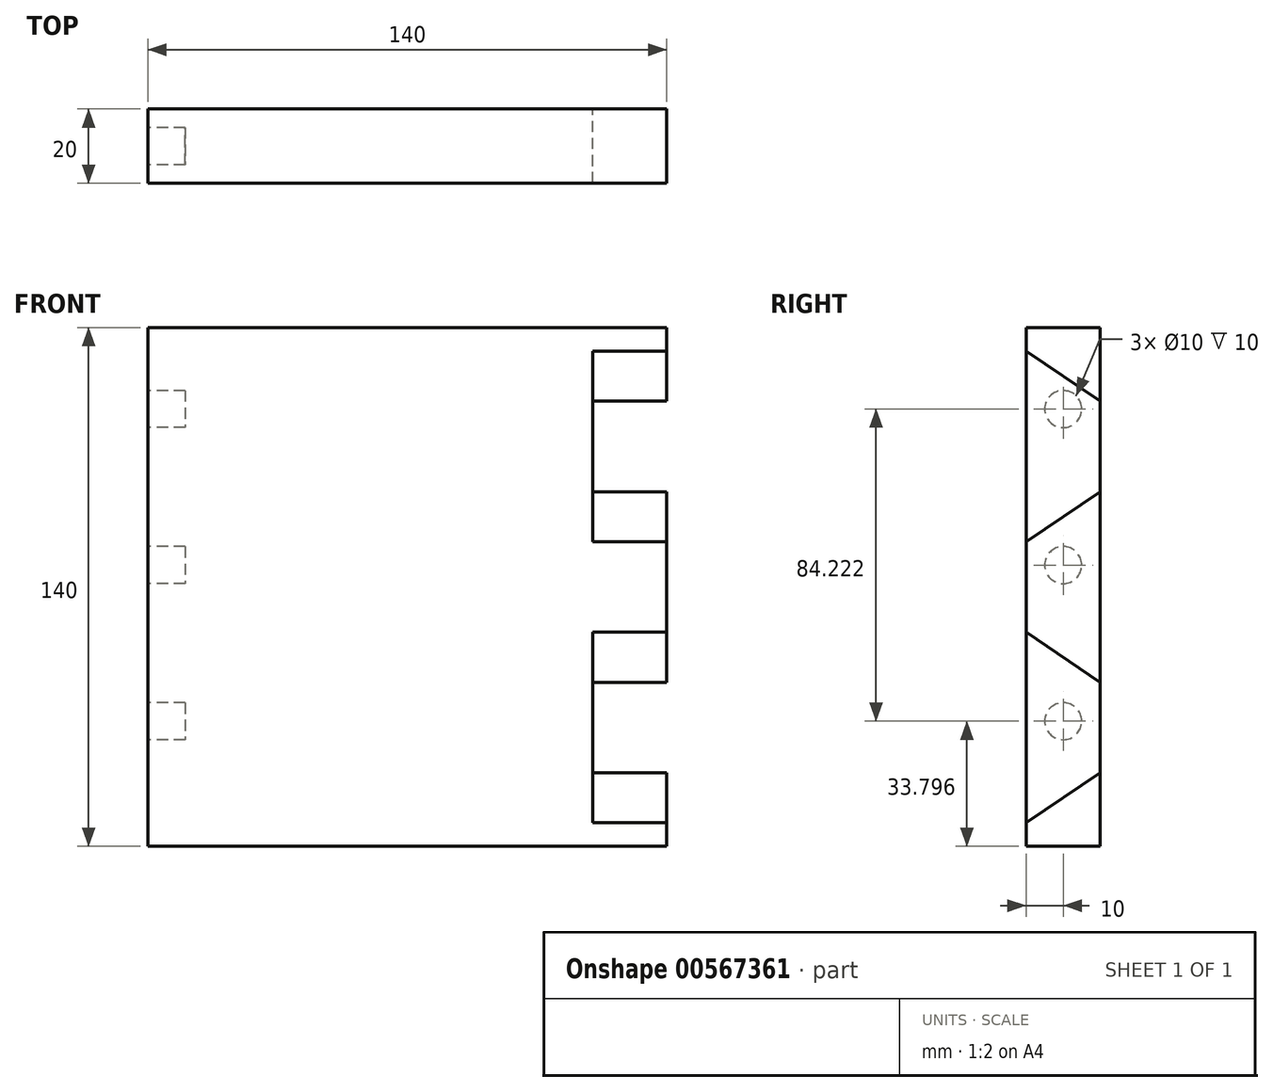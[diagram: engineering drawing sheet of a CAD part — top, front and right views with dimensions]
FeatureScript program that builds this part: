
annotation { "Feature Type Name" : "Feature", "Feature Type Description" : "" }
export const myFeature = defineFeature(function(context is Context, id is Id, definition is map)
    precondition{}
    {
        {
            var Q0;
            Q0=qCreatedBy(makeId("Front.planeOp"),FACE);
            var sketch = newSketch(context, id + "F0", { "sketchPlane" : qUnion([Q0])});
            skLineSegment(sketch, "E0.bottom", {"start": v(-140, 140) * mm, "end": v(0, 140) * mm});
            skLineSegment(sketch, "E0.top", {"start": v(-140, 0) * mm, "end": v(0, 0) * mm});
            skLineSegment(sketch, "E0.left", {"start": v(-140, 140) * mm, "end": v(-140, 0) * mm});
            skLineSegment(sketch, "E0.right", {"start": v(0, 140) * mm, "end": v(0, 0) * mm});
            skLineSegment(sketch, "E1.bottom", {"start": v(-140, 140) * mm, "end": v(-120, 140) * mm});
            skLineSegment(sketch, "E1.top", {"start": v(-140, 0) * mm, "end": v(-120, 0) * mm});
            skLineSegment(sketch, "E1.right", {"start": v(-120, 140) * mm, "end": v(-120, 0) * mm});
            skSolve(sketch);
        }
        {
            var Q0;
            Q0=makeQuery(id+"F0.imprint","IMPRINT",FACE,{"disambiguationData":[TD([[makeQuery(id+"F0.imprint","IMPRINT",EDGE,{"derivedFrom":sQuery(id+"F0.wireOp",EDGE,"E0.bottom")}),-1.0]])]});
            var Q1;
            Q1=makeQuery(id+"F0.imprint","IMPRINT",FACE,{"disambiguationData":[TD([[makeQuery(id+"F0.imprint","IMPRINT",EDGE,{"derivedFrom":sQuery(id+"F0.wireOp",EDGE,"E1.bottom")}),-1.0]])]});
            extrude(context, id + "F1", {"entities" : qUnion([Q0, Q1]), "depth" : 20 * mm, "offsetDistance" : 25 * mm});
        }
        {
            var Q0;
            Q0=makeQuery(id+"F1.opExtrude","SWEPT_FACE",FACE,{"disambiguationData":[OSD([sQuery(id+"F0.wireOp",EDGE,"E0.right")])]});
            var sketch = newSketch(context, id + "F2", { "sketchPlane" : qUnion([Q0])});
            skLineSegment(sketch, "E2", {"start": v(-20, 70) * mm, "end": v(0, 70) * mm});
            skLineSegment(sketch, "E3", {"start": v(-20, 82.22) * mm, "end": v(0, 95.72) * mm});
            skLineSegment(sketch, "E4", {"start": v(-20, 82.22) * mm, "end": v(-20, 70) * mm});
            skLineSegment(sketch, "E5", {"start": v(-20, 70) * mm, "end": v(-20, 57.78) * mm});
            skLineSegment(sketch, "E6", {"start": v(-20, 57.78) * mm, "end": v(0, 44.28) * mm});
            skLineSegment(sketch, "E7", {"start": v(-20, 82.22) * mm, "end": v(-20, 57.78) * mm});
            skLineSegment(sketch, "E8", {"start": v(0, 95.72) * mm, "end": v(0, 120.15) * mm});
            skLineSegment(sketch, "E9", {"start": v(0, 120.15) * mm, "end": v(-20, 133.65) * mm});
            skLineSegment(sketch, "E10.MirrorCS", {"start": v(0, 44.28) * mm, "end": v(0, 19.85) * mm});
            skLineSegment(sketch, "E11.MirrorCS", {"start": v(0, 19.85) * mm, "end": v(-20, 6.35) * mm});
            skLineSegment(sketch, "E12", {"start": v(-20, 133.65) * mm, "end": v(-20, 140) * mm});
            skLineSegment(sketch, "E13", {"start": v(-20, 140) * mm, "end": v(0, 140) * mm});
            skLineSegment(sketch, "E14", {"start": v(0, 140) * mm, "end": v(0, 120.15) * mm});
            skLineSegment(sketch, "E15", {"start": v(-20, 133.65) * mm, "end": v(-20, 82.22) * mm});
            skLineSegment(sketch, "E16", {"start": v(0, 95.72) * mm, "end": v(0, 70) * mm});
            skLineSegment(sketch, "E17", {"start": v(0, 44.28) * mm, "end": v(0, 70) * mm});
            skLineSegment(sketch, "E18", {"start": v(-20, 57.78) * mm, "end": v(-20, 6.35) * mm});
            skLineSegment(sketch, "E19", {"start": v(-20, 0) * mm, "end": v(-20, 6.35) * mm});
            skLineSegment(sketch, "E20", {"start": v(0, 0) * mm, "end": v(-20, 0) * mm});
            skLineSegment(sketch, "E21", {"start": v(0, 19.85) * mm, "end": v(0, 0) * mm});
            skSolve(sketch);
        }
        {
            var Q0;
            Q0=makeQuery(id+"F2.imprint","IMPRINT",FACE,{"disambiguationData":[TD([[makeQuery(id+"F2.imprint","IMPRINT",EDGE,{"derivedFrom":sQuery(id+"F2.wireOp",EDGE,"E3")}),1.0]])]});
            var Q1;
            Q1=makeQuery(id+"F2.imprint","IMPRINT",FACE,{"disambiguationData":[TD([[makeQuery(id+"F2.imprint","IMPRINT",EDGE,{"derivedFrom":sQuery(id+"F2.wireOp",EDGE,"E6")}),-1.0]])]});
            extrude(context, id + "F3", {"entities" : qUnion([Q0, Q1]), "operationType" : NewBodyOperationType.REMOVE, "oppositeDirection" : true, "depth" : 20 * mm, "offsetDistance" : 25 * mm});
        }
        {
            var Q0;
            Q0=makeQuery(id+"F1.opExtrude","SWEPT_FACE",FACE,{"disambiguationData":[OSD([sQuery(id+"F0.wireOp",EDGE,"E0.left")])]});
            var sketch = newSketch(context, id + "F4", { "sketchPlane" : qUnion([Q0])});
            skLineSegment(sketch, "E22", {"start": v(0, 75.9) * mm, "end": v(20, 75.9) * mm});
            skLineSegment(sketch, "E23", {"start": v(0, 33.8) * mm, "end": v(20, 33.8) * mm});
            skLineSegment(sketch, "E24.MirrorCS", {"start": v(0, 118.02) * mm, "end": v(20, 118.02) * mm});
            skCircle(sketch, "E25", {"center": v(10, 118.02) * mm, "radius": 5 * mm});
            skCircle(sketch, "E26", {"center": v(10, 75.9) * mm, "radius": 5 * mm});
            skCircle(sketch, "E27", {"center": v(10, 33.8) * mm, "radius": 5 * mm});
            skSolve(sketch);
        }
        {
            var Q0;
            Q0 = qSketchRegion(id + "F4", true);
            extrude(context, id + "F5", {"entities" : qUnion([Q0]), "operationType" : NewBodyOperationType.REMOVE, "oppositeDirection" : true, "depth" : 10 * mm, "offsetDistance" : 25 * mm});
        }
    });
